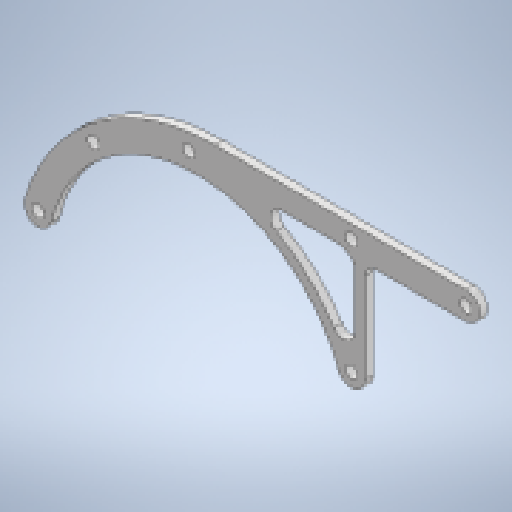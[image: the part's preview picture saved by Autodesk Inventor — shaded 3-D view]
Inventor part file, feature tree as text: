
AUTODESK INVENTOR PART (.ipt)
format: ipt  version: 2025.1 (Build 291241000, 241)  size: 216,576 bytes
history: native  units: mm
features: other x4, reference x4, extrude x3, sketch x3, fillet x2
ambient origin geometry x8: Origin, YZ Plane, XZ Plane, XY Plane, X Axis, Y Axis, Z Axis, Center Point
bodies: Body1 (feature_tree)
feature tree (16):
  other  "ソリッド1"
  extrude  "押し出し1"  Depth=5.0mm
  fillet  "フィレット1"  Radius=2.2mm
  extrude  "押し出し2"  Depth=2.2mm
  fillet  "フィレット2"  Radius=5.0mm
  extrude  "押し出し3"  Depth=5.0mm
  sketch  "スケッチ2"
  reference  "参照5"
  reference  "参照6"
  reference  "参照7"
  sketch  "スケッチ3"
  sketch  "スケッチ4"
  reference  "参照8"
  other  "<userpath>\Documents\Inventor\Vixen\doutai.iam"
  other  "doutai.iam"
  other  "KRS3300_scale:1"
